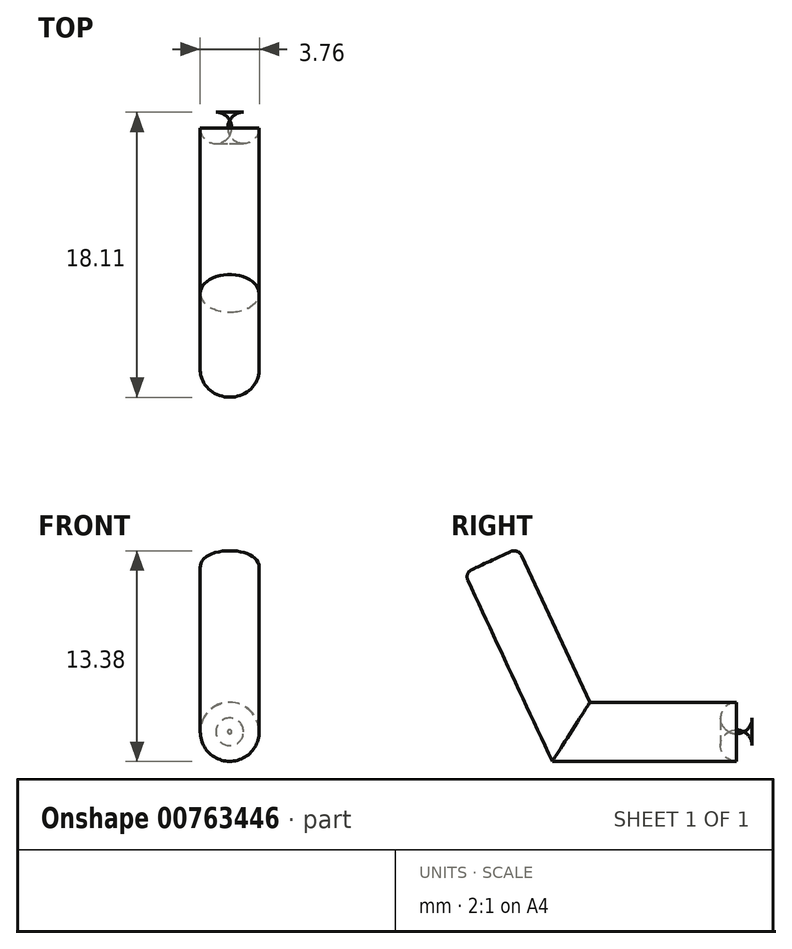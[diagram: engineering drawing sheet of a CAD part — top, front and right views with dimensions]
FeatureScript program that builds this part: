
annotation { "Feature Type Name" : "Feature", "Feature Type Description" : "" }
export const myFeature = defineFeature(function(context is Context, id is Id, definition is map)
    precondition{}
    {
        {
            var Q0;
            Q0=qCreatedBy(makeId("Front.planeOp"),FACE);
            var sketch = newSketch(context, id + "F0", { "sketchPlane" : qUnion([Q0])});
            skCircle(sketch, "E0", {"center": v(0, 0) * mm, "radius": 1.88 * mm});
            skSolve(sketch);
        }
        {
            var Q0;
            Q0=qCreatedBy(makeId("Right.planeOp"),FACE);
            var sketch = newSketch(context, id + "F1", { "sketchPlane" : qUnion([Q0])});
            skLineSegment(sketch, "E1", {"start": v(0, 0) * mm, "end": v(-11.5, 0) * mm});
            skLineSegment(sketch, "E2", {"start": v(-11.5, 0) * mm, "end": v(-16.57, 10.88) * mm});
            skSolve(sketch);
        }
        {
            var Q0;
            Q0=makeQuery(id+"F0.imprint","IMPRINT",FACE,{"disambiguationData":[TD([[makeQuery(id+"F0.imprint","IMPRINT",EDGE,{"derivedFrom":sQuery(id+"F0.wireOp",EDGE,"E0")}),1.0]])]});
            var Q1;
            Q1=sQuery(id+"F1.wireOp",EDGE,"E1");
            var Q2;
            Q2=sQuery(id+"F1.wireOp",EDGE,"E2");
            sweep(context, id + "F2", {"profiles" : qUnion([Q0]), "path" : qUnion([Q1, Q2])});
        }
        {
            var Q0;
            Q0=makeQuery(id+"F2.opSweep","CAP_EDGE",EDGE,{"disambiguationData":[OSD([sQuery(id+"F0.wireOp",EDGE,"E0"),sQuery(id+"F1.wireOp",VERTEX,"E1.start")])],"isStart":true});
            fillet(context, id + "F3", {"entities" : qUnion([Q0]), "radius" : 1 * mm, "tangentPropagation" : true, "allowEdgeOverflow" : false});
        }
        {
            var Q0;
            Q0=makeQuery(id+"F2.opSweep","CAP_EDGE",EDGE,{"disambiguationData":[OSD([sQuery(id+"F0.wireOp",EDGE,"E0"),sQuery(id+"F1.wireOp",VERTEX,"E2.end")])],"isStart":false});
            fillet(context, id + "F4", {"entities" : qUnion([Q0]), "radius" : .5 * mm, "tangentPropagation" : true, "allowEdgeOverflow" : false});
        }
    });
